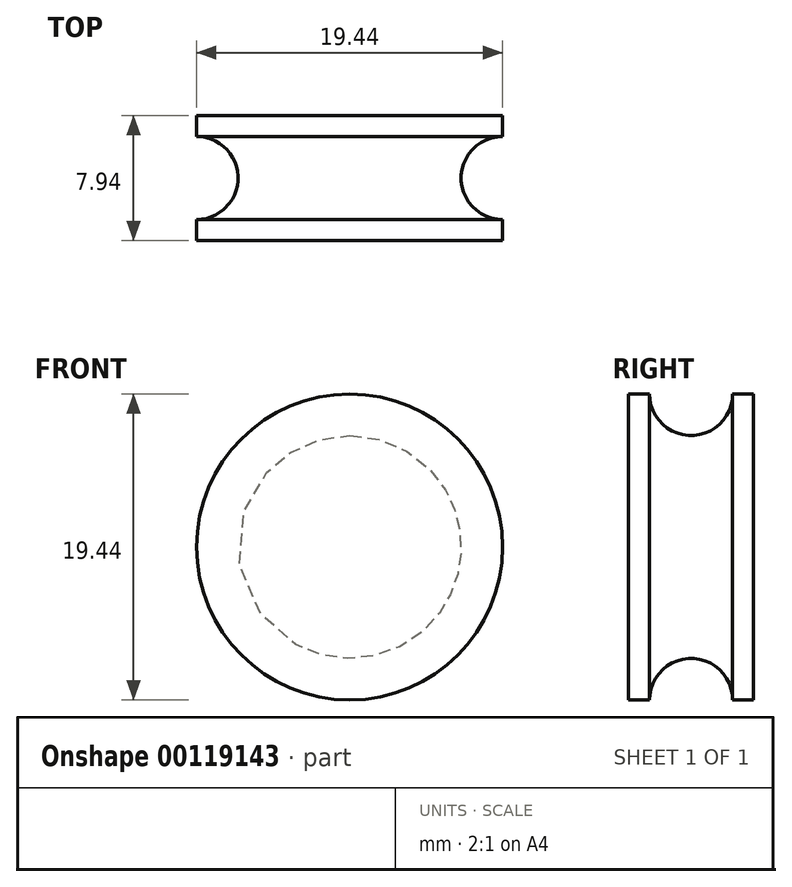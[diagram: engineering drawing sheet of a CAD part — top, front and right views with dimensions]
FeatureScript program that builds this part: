
annotation { "Feature Type Name" : "Feature", "Feature Type Description" : "" }
export const myFeature = defineFeature(function(context is Context, id is Id, definition is map)
    precondition{}
    {
        {
            var Q0;
            Q0=qCreatedBy(makeId("Front.planeOp"),FACE);
            var sketch = newSketch(context, id + "F0", { "sketchPlane" : qUnion([Q0])});
            skCircle(sketch, "E0", {"center": v(0, 0) * mm, "radius": 9.72 * mm});
            skSolve(sketch);
        }
        {
            var Q0;
            Q0 = qSketchRegion(id + "F0", true);
            extrude(context, id + "F1", {"entities" : qUnion([Q0]), "endBound" : BoundingType.SYMMETRIC, "depth" : 7.94 * mm});
        }
        {
            var Q0;
            Q0=qCreatedBy(makeId("Right.planeOp"),FACE);
            var sketch = newSketch(context, id + "F2", { "sketchPlane" : qUnion([Q0])});
            skLineSegment(sketch, "E1.0", {"start": v(-3.97, -9.72) * mm, "end": v(-3.97, 9.72) * mm, "construction": true});
            skLineSegment(sketch, "E1.1", {"start": v(3.97, -9.72) * mm, "end": v(3.97, 9.72) * mm, "construction": true});
            skLineSegment(sketch, "E2", {"start": v(-3.97, 9.72) * mm, "end": v(3.97, 9.72) * mm, "construction": true});
            skCircle(sketch, "E3", {"center": v(0, 9.72) * mm, "radius": 2.64 * mm});
            skLineSegment(sketch, "E4", {"start": v(-3.97, 0) * mm, "end": v(3.97, 0) * mm, "construction": true});
            skSolve(sketch);
        }
        {
            var Q0;
            Q0=makeQuery(id+"F2.imprint","IMPRINT",FACE,{"disambiguationData":[TD([[makeQuery(id+"F2.imprint","IMPRINT",EDGE,{"derivedFrom":sQuery(id+"F2.wireOp",EDGE,"E3")}),1.0]])]});
            var Q1;
            Q1=sQuery(id+"F2.wireOp",EDGE,"E4");
            revolve(context, id + "F3", {"operationType" : NewBodyOperationType.REMOVE, "entities" : qUnion([Q0]), "axis" : qUnion([Q1]), "revolveType" : RevolveType.FULL, "oppositeDirection" : true});
        }
    });
